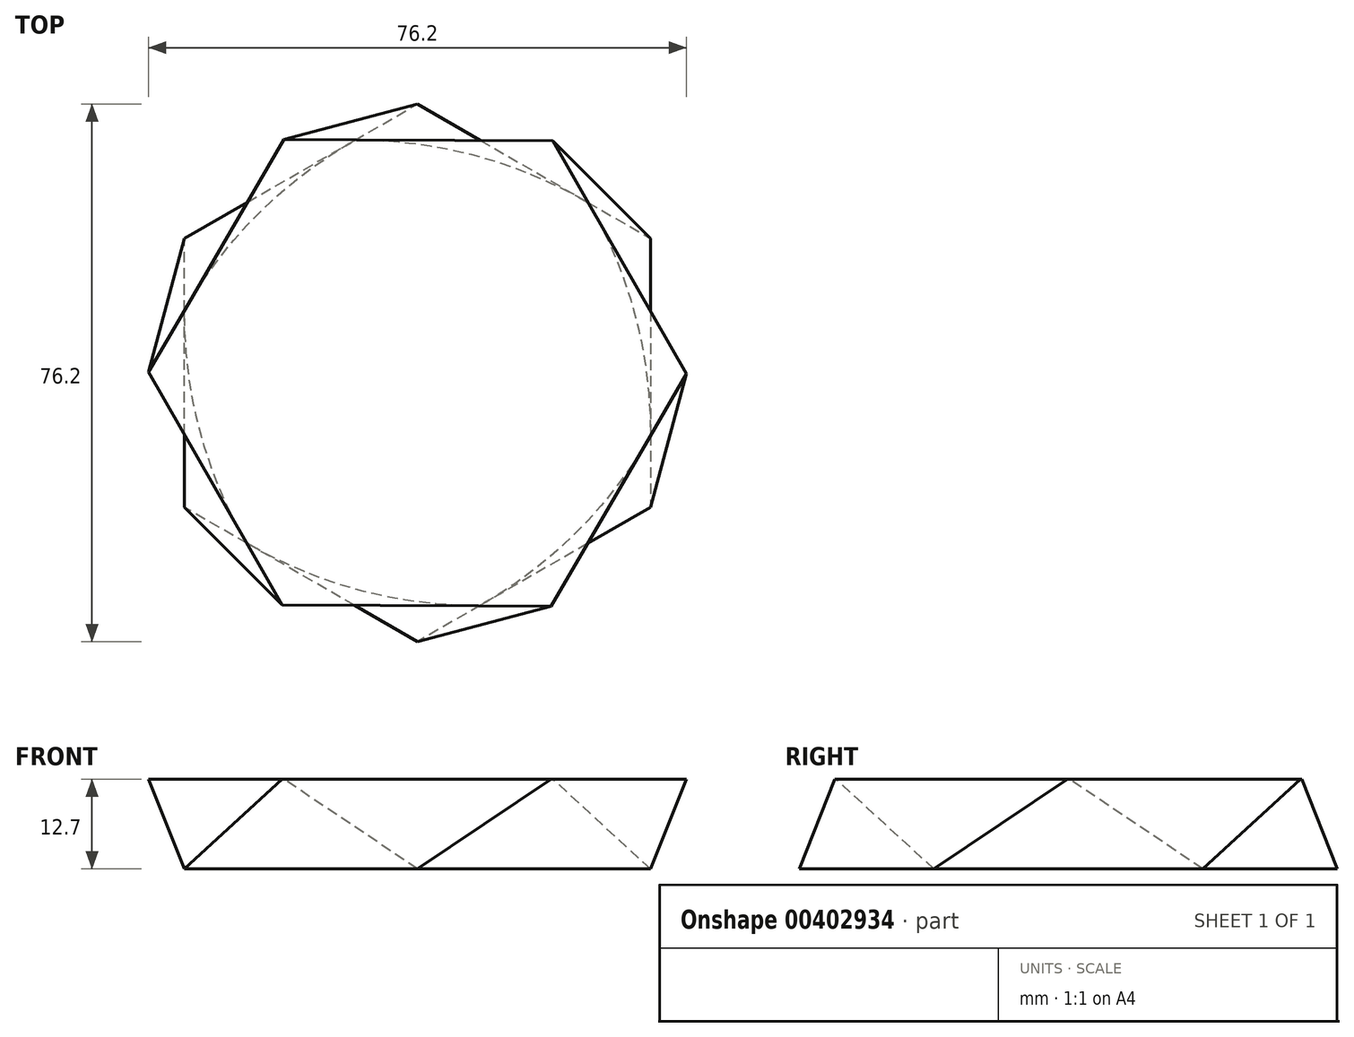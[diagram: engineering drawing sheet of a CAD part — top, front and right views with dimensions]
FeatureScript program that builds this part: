
annotation { "Feature Type Name" : "Feature", "Feature Type Description" : "" }
export const myFeature = defineFeature(function(context is Context, id is Id, definition is map)
    precondition{}
    {
        {
            var Q0;
            Q0=qCreatedBy(makeId("Top.planeOp"),FACE);
            var sketch = newSketch(context, id + "F0", { "sketchPlane" : qUnion([Q0])});
            skCircle(sketch, "E0.cCircle", {"center": v(0, 0) * mm, "radius": 33 * mm, "construction": true});
            skLineSegment(sketch, "E0.0", {"start": v(33, 19.05) * mm, "end": v(33, -19.05) * mm});
            skLineSegment(sketch, "E0.1", {"start": v(33, -19.05) * mm, "end": v(0, -38.1) * mm});
            skLineSegment(sketch, "E0.2", {"start": v(0, -38.1) * mm, "end": v(-33, -19.05) * mm});
            skLineSegment(sketch, "E0.3", {"start": v(-33, -19.05) * mm, "end": v(-33, 19.05) * mm});
            skLineSegment(sketch, "E0.4", {"start": v(-33, 19.05) * mm, "end": v(0, 38.1) * mm});
            skLineSegment(sketch, "E0.5", {"start": v(0, 38.1) * mm, "end": v(33, 19.05) * mm});
            skPoint(sketch, "E0.0.midPoint", {"position": v(33, 0) * mm});
            skSolve(sketch);
        }
        {
            var Q0;
            Q0=qCreatedBy(makeId("Top.planeOp"),FACE);
            cPlane(context, id + "F1", {"entities" : qUnion([Q0]), "cplaneType" : CPlaneType.OFFSET, "offset" : 12.7 * mm, "width" : 152.4 * mm, "height" : 152.4 * mm});
        }
        {
            var Q0;
            Q0=qCreatedBy(id+"F1.planeOp",FACE);
            var sketch = newSketch(context, id + "F2", { "sketchPlane" : qUnion([Q0])});
            skCircle(sketch, "E1.cCircle", {"center": v(0, 0) * mm, "radius": 33 * mm, "construction": true});
            skLineSegment(sketch, "E1.0", {"start": v(19.18, 32.92) * mm, "end": v(38.1, -0.15) * mm});
            skLineSegment(sketch, "E1.1", {"start": v(38.1, -0.15) * mm, "end": v(18.92, -33.07) * mm});
            skLineSegment(sketch, "E1.2", {"start": v(18.92, -33.07) * mm, "end": v(-19.18, -32.92) * mm});
            skLineSegment(sketch, "E1.3", {"start": v(-19.18, -32.92) * mm, "end": v(-38.1, 0.15) * mm});
            skLineSegment(sketch, "E1.4", {"start": v(-38.1, 0.15) * mm, "end": v(-18.92, 33.07) * mm});
            skLineSegment(sketch, "E1.5", {"start": v(-18.92, 33.07) * mm, "end": v(19.18, 32.92) * mm});
            skPoint(sketch, "E1.0.midPoint", {"position": v(28.64, 16.38) * mm});
            skSolve(sketch);
        }
        {
            var Q0;
            Q0=makeQuery(id+"F0.imprint","IMPRINT",FACE,{"disambiguationData":[TD([[makeQuery(id+"F0.imprint","IMPRINT",EDGE,{"derivedFrom":sQuery(id+"F0.wireOp",EDGE,"E0.0")}),-1.0]])]});
            var Q1;
            Q1=makeQuery(id+"F2.imprint","IMPRINT",FACE,{"disambiguationData":[TD([[makeQuery(id+"F2.imprint","IMPRINT",EDGE,{"derivedFrom":sQuery(id+"F2.wireOp",EDGE,"E1.0")}),-1.0]])]});
            loft(context, id + "F3", {"sheetProfilesArray" : [{ "sheetProfileEntities" : qUnion([Q0]) }, { "sheetProfileEntities" : qUnion([Q1]) }]});
        }
    });
